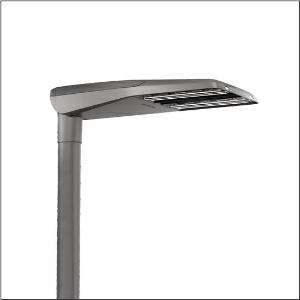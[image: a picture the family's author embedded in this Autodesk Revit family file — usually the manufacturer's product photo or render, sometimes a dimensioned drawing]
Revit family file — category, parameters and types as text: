
# Revit family: streetlight_sl_11_iq_midi___st1_2a_5xc3a51e08me_cf1e
name_source: partatom
category: Lighting Fixtures
units: mm (PartAtom-declared; Revit-internal decimal feet)

## family parameters
Cut with Voids When Loaded = No
Host = Face
Light Source = No
Part Type = Normal
Room Calculation Point = No
Round Connector Dimension = Use Diameter
Shared = No

## types (1)
- --- (1 x LED, 18110 lm, 124.7 W, 3000K)
    Apparent Load = 125 VA
    CIE Flux Codes = 32 70 96 100 100
    Color Rendering = 70
    Color Temperature = 3000K
    Default Elevation = 1800 mm
    Description = Streetlight SL 11 iQ midi, mast luminaire, primary light control with 3 zone facetted reflector, of plastic, silver coated, highly specular, primary optical cover: cover, of PMMA, transparent, light distribution: ST1.2a, light emission: direct distribution, primary light characteristic: asymmetric, installation type: post-top, side-entry, LED, High Power LED, rated luminous flux: 18.110lm, luminous efficacy: 145lm/W, light colour: 730, colour temperature: 3000K, control: optimised constant luminous flux control (CLO 2.0), Desk-Remote (wireless, voltage-free reading and setting of iQ features in the workshop via application-optimized NFC function/RFID function), Light-Fading, Smart-Wire, Night-Set, Lumen-Switch, Temp-Guard, Auto-Match, with cable H07RN-F 5x 1.5mm², mains connection: 230..240V, AC, 50/60Hz, connection cable pre-assembled, cable length: 12,5m, start of lifetime: 125W, end of service life: 132W, reduction: 57W, luminaire housing, of diecast aluminium, powder-coated, Siteco® metallic grey (DB 702S), please order mast flange separately, inclination adjustable without tools: 0°, 5°, 10°, 15° (post-top) | 0°, -5°, -10°, -15° (side-entry), sealing non-destructively replaceable, multi-level sealing system, length: 780mm, width: 376mm, height: 118mm, mast flange for spigot size: 42mm (side-entry): 5XC10008XM4, 60/48mm (side-entry/post-top): 5XC10108XM2, 76/60mm (side-entry/post-top): 5XC10108XM1, equipment: Power, protection rating (complete): IP66, insulation class (complete): insulation class II (safety insulation), certification: CE, ENEC, VDE, impact resistance: IK09, permissible operating ambient temperature for outdoor applications: -25..+50°C, standard-compliant lighting for roads and squares, Environmental Product Declaration (EPD) tested and certified by an independent institute, packaging unit: 1 piece

Light Distribution: ST1.2a
    Height = 118 mm
    Lamp = 1 x LED
    Lamp Light Flux = 18110 lm
    Lamp Power = 124.7 W
    Lamp count = 1
    Length = 780 mm
    Luminous efficacy = 145 lm/W
    Manufacturer = Siteco
    ModVariant = No
    Model = 5XC3A51E08ME
    Number of Poles = 1
    OnlyDefault = Yes
    Power Factor = 1
    Product Name = Streetlight SL 11 iQ midi | ST1.2a
    Product group = mast luminaire | pylon top
    ProductGroupID = 6100
    Protection Class = Protection class II
    Protection Degree = IP 66
    RLX_Detail_Level = 1
    RLX_Emergency_Light_Flux = 0 lm
    RLX_Emergency_Type = 0
    RLX_Emergency_Type_DB = No
    RlxData = <blob elided: 70797 chars, md5=83aeaae1>
    Socket = socket
    Standby Power = 0 W
    System Light Flux = 18110 lm
    System Power = 125 W
    Type Comments = factory setting: luminous flux: 100 % | dim-lin: 254 | 557 mA
    Type Image = l_1005960.jpg
    URL = http://relux.com
    VarID = @adj_149741
    Voltage = 0 V
    Weight = 0.00 kg
    Width = 376 mm

## geometry (parser evidence)
native form markers: Blend x4, Sweep x9
no freeform markers — native parametric forms only
